# Revit family: Legrand XL³-S 160 empotrada
name_source: partatom
category: Equipement électrique
units: mm (PartAtom-declared; Revit-internal decimal feet)

## family parameters
Basée sur le plan de construction = Non
Configuration du panneau = Deux colonnes, circuits au sein
Cote de connecteur circulaire = Utiliser le diamètre
Couper avec des vides une fois chargée = Non
Numéro OmniClass = 23.80.30.11.17
Partagée = Non
Point de calcul de pièce = Non
Titre OmniClass = Distribution Boards and Control Panels
Toujours verticalement = Oui
Type d'élément = Tableau de raccordement

## types (12) — shared parameters
Condiciones Generales de Uso = https://export.legrand.com
ETIM Class 6.0 = EC000261
Fabricant = Legrand
IK = 07
IP = 40
Image du type = XL3S160_encastre_337224_p_231245.jpg
Materia = Acero
RAL = 9003
URL = www.legrand.fr
distancia lado asentamiento = 138 mm  [stored 0.452756 ft]
peso = 0.00 kg
profundidad = 138 mm  [stored 0.452756 ft]
profundidad Empotrado = 116 mm  [stored 0.380577 ft]
puerta = Oui
zero-valued in all types: Elévation par défaut

## per-type parameters (varying)
- Envolvente de distribución - XL³ S 160 -  Metal - caja empotrada - 24 módulos - 2 filas: Altura 1=512 mm  [stored 1.67979 ft]; Altura 2=440 mm  [stored 1.44357 ft]; Caja 337222=Oui; Caja 337223=Non; Caja 337224=Non; Caja 337225=Non; Caja 337226=Non; Caja 337227=Non; Caja 337228=Non; Caja 337234=Non; Caja 337235=Non; Caja 337236=Non; Caja 337237=Non; Caja 337238=Non; Description=337222  Envolvente de distribución - XL³ S 160 -  Metal - caja empotrada - 24 módulos - 2 filas; anchura=667 mm  [stored 2.18832 ft]; anchura asentamiento=943 mm  [stored 3.09383 ft]; distancia antes de asentamiento=667 mm  [stored 2.18832 ft]; módulo (24 o 36)=24; número fila=2; profundidad asentamiento=805 mm  [stored 2.64108 ft]; puerta 337252=Oui; puerta 337253=Non; puerta 337254=Non; puerta 337255=Non; puerta 337256=Non; puerta 337257=Non; puerta 337258=Non; puerta 337264=Non; puerta 337265=Non; puerta 337266=Non; puerta 337267=Non; puerta 337268=Non
- Envolvente de distribución - XL³ S 160 -  Metal - caja empotrada - 24 módulos - 3 filas: Altura 1=662 mm  [stored 2.17192 ft]; Altura 2=590 mm  [stored 1.9357 ft]; Caja 337222=Non; Caja 337223=Oui; Caja 337224=Non; Caja 337225=Non; Caja 337226=Non; Caja 337227=Non; Caja 337228=Non; Caja 337234=Non; Caja 337235=Non; Caja 337236=Non; Caja 337237=Non; Caja 337238=Non; Description=337223  Envolvente de distribución - XL³ S 160 -  Metal - caja empotrada - 24 módulos - 3 filas; anchura=667 mm  [stored 2.18832 ft]; anchura asentamiento=943 mm  [stored 3.09383 ft]; distancia antes de asentamiento=667 mm  [stored 2.18832 ft]; módulo (24 o 36)=24; número fila=3; profundidad asentamiento=805 mm  [stored 2.64108 ft]; puerta 337252=Non; puerta 337253=Oui; puerta 337254=Non; puerta 337255=Non; puerta 337256=Non; puerta 337257=Non; puerta 337258=Non; puerta 337264=Non; puerta 337265=Non; puerta 337266=Non; puerta 337267=Non; puerta 337268=Non
- Envolvente de distribución - XL³ S 160 -  Metal - caja empotrada - 24 módulos - 4 filas: Altura 1=812 mm  [stored 2.66404 ft]; Altura 2=740 mm  [stored 2.42782 ft]; Caja 337222=Non; Caja 337223=Non; Caja 337224=Oui; Caja 337225=Non; Caja 337226=Non; Caja 337227=Non; Caja 337228=Non; Caja 337234=Non; Caja 337235=Non; Caja 337236=Non; Caja 337237=Non; Caja 337238=Non; Description=337224  Envolvente de distribución - XL³ S 160 -  Metal - caja empotrada - 24 módulos - 4 filas; anchura=667 mm  [stored 2.18832 ft]; anchura asentamiento=943 mm  [stored 3.09383 ft]; distancia antes de asentamiento=667 mm  [stored 2.18832 ft]; módulo (24 o 36)=24; número fila=4; profundidad asentamiento=805 mm  [stored 2.64108 ft]; puerta 337252=Non; puerta 337253=Non; puerta 337254=Oui; puerta 337255=Non; puerta 337256=Non; puerta 337257=Non; puerta 337258=Non; puerta 337264=Non; puerta 337265=Non; puerta 337266=Non; puerta 337267=Non; puerta 337268=Non
- Envolvente de distribución - XL³ S 160 -  Metal - caja empotrada - 24 módulos - 5 filas: Altura 1=962 mm  [stored 3.15617 ft]; Altura 2=890 mm  [stored 2.91995 ft]; Caja 337222=Non; Caja 337223=Non; Caja 337224=Non; Caja 337225=Oui; Caja 337226=Non; Caja 337227=Non; Caja 337228=Non; Caja 337234=Non; Caja 337235=Non; Caja 337236=Non; Caja 337237=Non; Caja 337238=Non; Description=337225  Envolvente de distribución - XL³ S 160 -  Metal - caja empotrada - 24 módulos - 5 filas; anchura=667 mm  [stored 2.18832 ft]; anchura asentamiento=943 mm  [stored 3.09383 ft]; distancia antes de asentamiento=667 mm  [stored 2.18832 ft]; módulo (24 o 36)=24; número fila=5; profundidad asentamiento=805 mm  [stored 2.64108 ft]; puerta 337252=Non; puerta 337253=Non; puerta 337254=Non; puerta 337255=Oui; puerta 337256=Non; puerta 337257=Non; puerta 337258=Non; puerta 337264=Non; puerta 337265=Non; puerta 337266=Non; puerta 337267=Non; puerta 337268=Non
- Envolvente de distribución - XL³ S 160 -  Metal - caja empotrada - 24 módulos - 6 filas: Altura 1=1112 mm  [stored 3.64829 ft]; Altura 2=1040 mm  [stored 3.41207 ft]; Caja 337222=Non; Caja 337223=Non; Caja 337224=Non; Caja 337225=Non; Caja 337226=Oui; Caja 337227=Non; Caja 337228=Non; Caja 337234=Non; Caja 337235=Non; Caja 337236=Non; Caja 337237=Non; Caja 337238=Non; Description=337226  Envolvente de distribución - XL³ S 160 -  Metal - caja empotrada - 24 módulos - 6 filas; anchura=667 mm  [stored 2.18832 ft]; anchura asentamiento=943 mm  [stored 3.09383 ft]; distancia antes de asentamiento=667 mm  [stored 2.18832 ft]; módulo (24 o 36)=24; número fila=6; profundidad asentamiento=805 mm  [stored 2.64108 ft]; puerta 337252=Non; puerta 337253=Non; puerta 337254=Non; puerta 337255=Non; puerta 337256=Oui; puerta 337257=Non; puerta 337258=Non; puerta 337264=Non; puerta 337265=Non; puerta 337266=Non; puerta 337267=Non; puerta 337268=Non
- Envolvente de distribución - XL³ S 160 -  Metal - caja empotrada - 24 módulos - 7 filas: Altura 1=1262 mm  [stored 4.14042 ft]; Altura 2=1190 mm  [stored 3.9042 ft]; Caja 337222=Non; Caja 337223=Non; Caja 337224=Non; Caja 337225=Non; Caja 337226=Non; Caja 337227=Oui; Caja 337228=Non; Caja 337234=Non; Caja 337235=Non; Caja 337236=Non; Caja 337237=Non; Caja 337238=Non; Description=337227  Envolvente de distribución - XL³ S 160 -  Metal - caja empotrada - 24 módulos - 7 filas; anchura=667 mm  [stored 2.18832 ft]; anchura asentamiento=943 mm  [stored 3.09383 ft]; distancia antes de asentamiento=667 mm  [stored 2.18832 ft]; módulo (24 o 36)=24; número fila=7; profundidad asentamiento=805 mm  [stored 2.64108 ft]; puerta 337252=Non; puerta 337253=Non; puerta 337254=Non; puerta 337255=Non; puerta 337256=Non; puerta 337257=Oui; puerta 337258=Non; puerta 337264=Non; puerta 337265=Non; puerta 337266=Non; puerta 337267=Non; puerta 337268=Non
- Envolvente de distribución - XL³ S 160 -  Metal - caja empotrada - 24 módulos - 8 filas: Altura 1=1412 mm  [stored 4.63255 ft]; Altura 2=1340 mm  [stored 4.39633 ft]; Caja 337222=Non; Caja 337223=Non; Caja 337224=Non; Caja 337225=Non; Caja 337226=Non; Caja 337227=Non; Caja 337228=Oui; Caja 337234=Non; Caja 337235=Non; Caja 337236=Non; Caja 337237=Non; Caja 337238=Non; Description=337228  Envolvente de distribución - XL³ S 160 -  Metal - caja empotrada - 24 módulos - 8 filas; anchura=667 mm  [stored 2.18832 ft]; anchura asentamiento=943 mm  [stored 3.09383 ft]; distancia antes de asentamiento=667 mm  [stored 2.18832 ft]; módulo (24 o 36)=24; número fila=8; profundidad asentamiento=805 mm  [stored 2.64108 ft]; puerta 337252=Non; puerta 337253=Non; puerta 337254=Non; puerta 337255=Non; puerta 337256=Non; puerta 337257=Non; puerta 337258=Oui; puerta 337264=Non; puerta 337265=Non; puerta 337266=Non; puerta 337267=Non; puerta 337268=Non
- Envolvente de distribución - XL³ S 160 -  Metal - caja empotrada - 36 módulos - 4 filas: Altura 1=812 mm  [stored 2.66404 ft]; Altura 2=740 mm  [stored 2.42782 ft]; Caja 337222=Non; Caja 337223=Non; Caja 337224=Non; Caja 337225=Non; Caja 337226=Non; Caja 337227=Non; Caja 337228=Non; Caja 337234=Oui; Caja 337235=Non; Caja 337236=Non; Caja 337237=Non; Caja 337238=Non; Description=337234  Envolvente de distribución - XL³ S 160 -  Metal - caja empotrada - 36 módulos - 4 filas; anchura=883 mm  [stored 2.89698 ft]; anchura asentamiento=1159 mm; distancia antes de asentamiento=883 mm  [stored 2.89698 ft]; módulo (24 o 36)=36; número fila=4; profundidad asentamiento=1021 mm  [stored 3.34974 ft]; puerta 337252=Non; puerta 337253=Non; puerta 337254=Non; puerta 337255=Non; puerta 337256=Non; puerta 337257=Non; puerta 337258=Non; puerta 337264=Oui; puerta 337265=Non; puerta 337266=Non; puerta 337267=Non; puerta 337268=Non
- Envolvente de distribución - XL³ S 160 -  Metal - caja empotrada - 36 módulos - 5 filas: Altura 1=962 mm  [stored 3.15617 ft]; Altura 2=890 mm  [stored 2.91995 ft]; Caja 337222=Non; Caja 337223=Non; Caja 337224=Non; Caja 337225=Non; Caja 337226=Non; Caja 337227=Non; Caja 337228=Non; Caja 337234=Non; Caja 337235=Oui; Caja 337236=Non; Caja 337237=Non; Caja 337238=Non; Description=337235  Envolvente de distribución - XL³ S 160 -  Metal - caja empotrada - 36 módulos - 5 filas; anchura=883 mm  [stored 2.89698 ft]; anchura asentamiento=1159 mm; distancia antes de asentamiento=883 mm  [stored 2.89698 ft]; módulo (24 o 36)=36; número fila=5; profundidad asentamiento=1021 mm  [stored 3.34974 ft]; puerta 337252=Non; puerta 337253=Non; puerta 337254=Non; puerta 337255=Non; puerta 337256=Non; puerta 337257=Non; puerta 337258=Non; puerta 337264=Non; puerta 337265=Oui; puerta 337266=Non; puerta 337267=Non; puerta 337268=Non
- Envolvente de distribución - XL³ S 160 -  Metal - caja empotrada - 36 módulos - 6 filas: Altura 1=1112 mm  [stored 3.64829 ft]; Altura 2=1040 mm  [stored 3.41207 ft]; Caja 337222=Non; Caja 337223=Non; Caja 337224=Non; Caja 337225=Non; Caja 337226=Non; Caja 337227=Non; Caja 337228=Non; Caja 337234=Non; Caja 337235=Non; Caja 337236=Oui; Caja 337237=Non; Caja 337238=Non; Description=337236  Envolvente de distribución - XL³ S 160 -  Metal - caja empotrada - 36 módulos - 6 filas; anchura=883 mm  [stored 2.89698 ft]; anchura asentamiento=1159 mm; distancia antes de asentamiento=883 mm  [stored 2.89698 ft]; módulo (24 o 36)=36; número fila=6; profundidad asentamiento=1021 mm  [stored 3.34974 ft]; puerta 337252=Non; puerta 337253=Non; puerta 337254=Non; puerta 337255=Non; puerta 337256=Non; puerta 337257=Non; puerta 337258=Non; puerta 337264=Non; puerta 337265=Non; puerta 337266=Oui; puerta 337267=Non; puerta 337268=Non
- Envolvente de distribución - XL³ S 160 -  Metal - caja empotrada - 36 módulos - 7 filas: Altura 1=1262 mm  [stored 4.14042 ft]; Altura 2=1190 mm  [stored 3.9042 ft]; Caja 337222=Non; Caja 337223=Non; Caja 337224=Non; Caja 337225=Non; Caja 337226=Non; Caja 337227=Non; Caja 337228=Non; Caja 337234=Non; Caja 337235=Non; Caja 337236=Non; Caja 337237=Oui; Caja 337238=Non; Description=337237  Envolvente de distribución - XL³ S 160 -  Metal - caja empotrada - 36 módulos - 7 filas; anchura=883 mm  [stored 2.89698 ft]; anchura asentamiento=1159 mm; distancia antes de asentamiento=883 mm  [stored 2.89698 ft]; módulo (24 o 36)=36; número fila=7; profundidad asentamiento=1021 mm  [stored 3.34974 ft]; puerta 337252=Non; puerta 337253=Non; puerta 337254=Non; puerta 337255=Non; puerta 337256=Non; puerta 337257=Non; puerta 337258=Non; puerta 337264=Non; puerta 337265=Non; puerta 337266=Non; puerta 337267=Oui; puerta 337268=Non
- Envolvente de distribución - XL³ S 160 -  Metal - caja empotrada- 36 módulos - 8 filas: Altura 1=1412 mm  [stored 4.63255 ft]; Altura 2=1340 mm  [stored 4.39633 ft]; Caja 337222=Non; Caja 337223=Non; Caja 337224=Non; Caja 337225=Non; Caja 337226=Non; Caja 337227=Non; Caja 337228=Non; Caja 337234=Non; Caja 337235=Non; Caja 337236=Non; Caja 337237=Non; Caja 337238=Oui; Description=337238  Envolvente de distribución - XL³ S 160 -  Metal - caja empotrada- 36 módulos - 8 filas; anchura=883 mm  [stored 2.89698 ft]; anchura asentamiento=1159 mm; distancia antes de asentamiento=883 mm  [stored 2.89698 ft]; módulo (24 o 36)=36; número fila=8; profundidad asentamiento=1021 mm  [stored 3.34974 ft]; puerta 337252=Non; puerta 337253=Non; puerta 337254=Non; puerta 337255=Non; puerta 337256=Non; puerta 337257=Non; puerta 337258=Non; puerta 337264=Non; puerta 337265=Non; puerta 337266=Non; puerta 337267=Non; puerta 337268=Oui

note: [stored X ft] marks values corroborated as IEEE doubles in the binary element streams (Revit-internal decimal feet)
